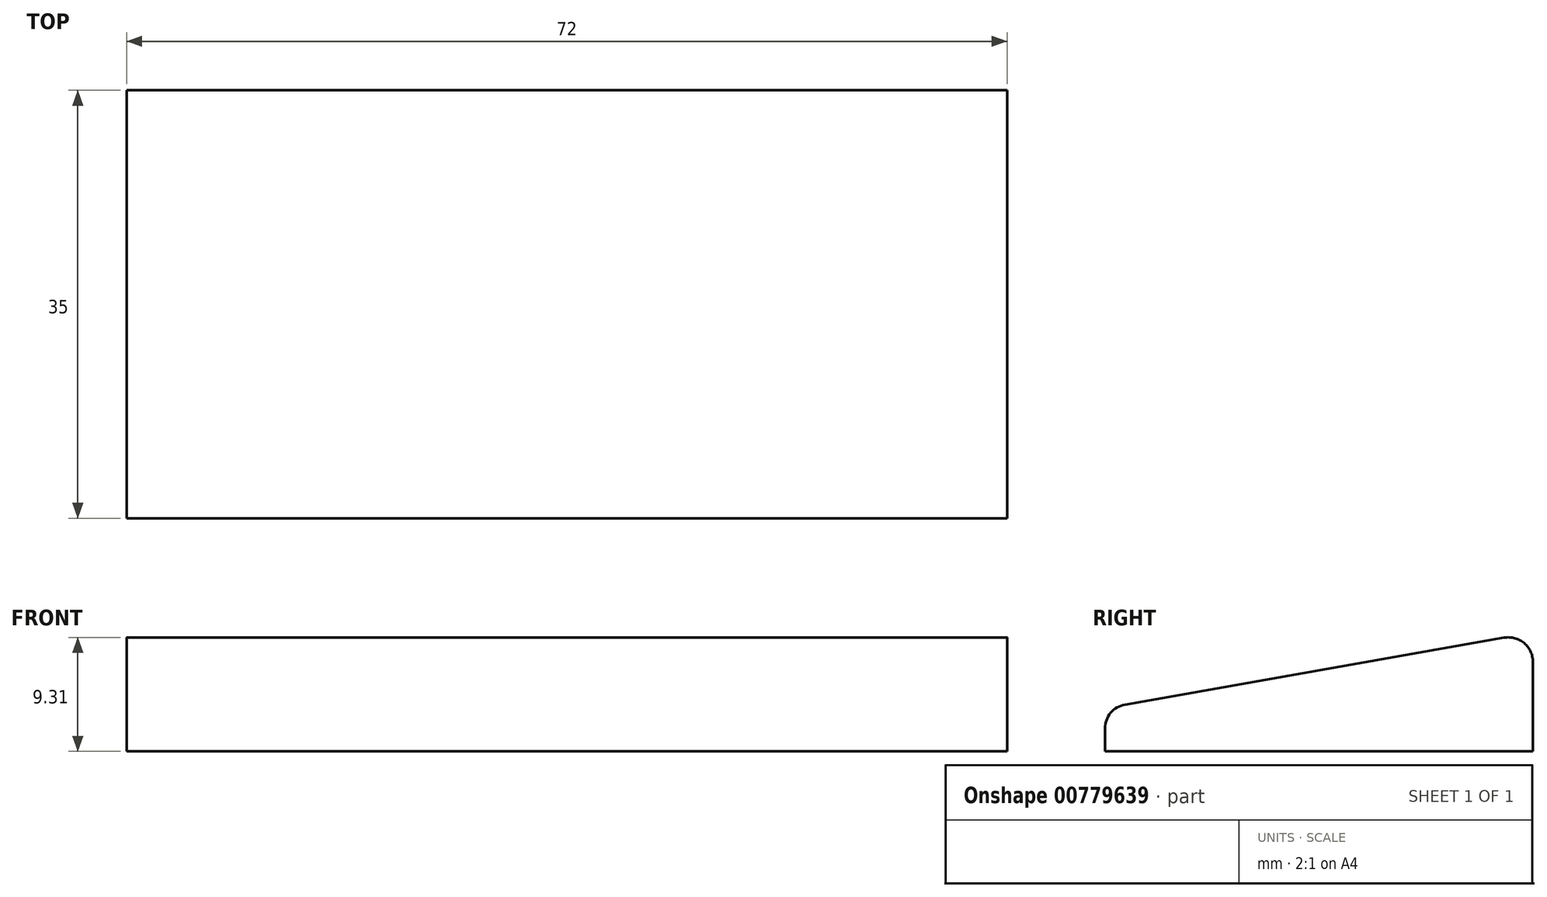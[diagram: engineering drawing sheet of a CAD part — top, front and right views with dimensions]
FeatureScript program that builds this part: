
annotation { "Feature Type Name" : "Feature", "Feature Type Description" : "" }
export const myFeature = defineFeature(function(context is Context, id is Id, definition is map)
    precondition{}
    {
        {
            var Q0;
            Q0=qCreatedBy(makeId("Right.planeOp"),FACE);
            var sketch = newSketch(context, id + "F0", { "sketchPlane" : qUnion([Q0])});
            skLineSegment(sketch, "E0", {"start": v(20, 0) * mm, "end": v(55, 0) * mm});
            skLineSegment(sketch, "E1", {"start": v(55, 0) * mm, "end": v(55, 9.7) * mm});
            skLineSegment(sketch, "E2", {"start": v(55, 9.7) * mm, "end": v(20, 3.53) * mm});
            skLineSegment(sketch, "E3", {"start": v(20, 0) * mm, "end": v(20, 3.53) * mm});
            skPoint(sketch, "E4.orphan", {"position": v(0, 0) * mm});
            skSolve(sketch);
        }
        {
            var Q0;
            Q0=qSketchRegion(id+"F0",true);
            extrude(context, id + "F1", {"entities" : qUnion([Q0]), "depth" : 72 * mm});
        }
        {
            var Q0;
            Q0=makeQuery(id+"F1.opExtrude","SWEPT_EDGE",EDGE,{"disambiguationData":[OSD([sQuery(id+"F0.wireOp",EDGE,"E1"),sQuery(id+"F0.wireOp",EDGE,"E2")])]});
            var Q1;
            Q1=makeQuery(id+"F1.opExtrude","SWEPT_EDGE",EDGE,{"disambiguationData":[OSD([sQuery(id+"F0.wireOp",EDGE,"E2"),sQuery(id+"F0.wireOp",EDGE,"E3")])]});
            fillet(context, id + "F2", {"entities" : qUnion([Q0, Q1]), "radius" : 2 * mm, "tangentPropagation" : true, "allowEdgeOverflow" : false});
        }
    });
